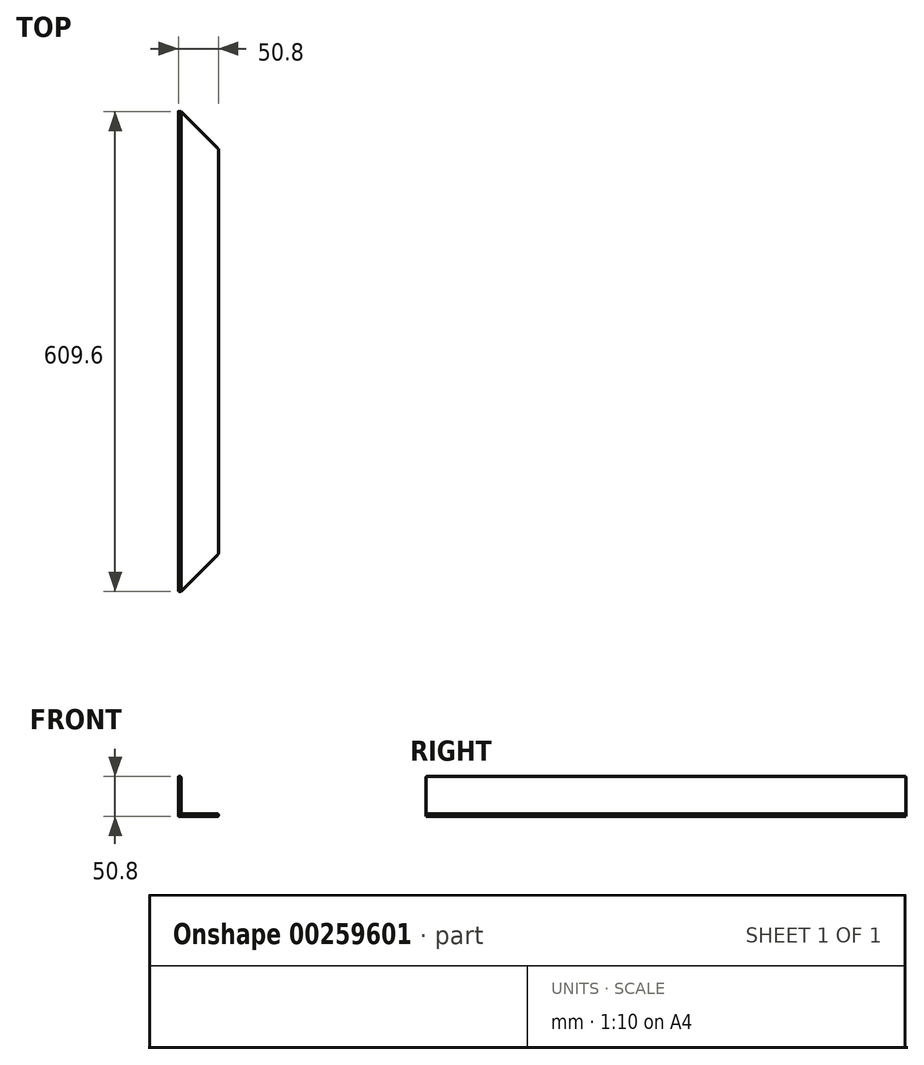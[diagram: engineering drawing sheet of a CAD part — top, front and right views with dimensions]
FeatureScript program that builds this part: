
annotation { "Feature Type Name" : "Feature", "Feature Type Description" : "" }
export const myFeature = defineFeature(function(context is Context, id is Id, definition is map)
    precondition{}
    {
        {
            var Q0;
            Q0=qCreatedBy(makeId("Front.planeOp"),FACE);
            var sketch = newSketch(context, id + "F0", { "sketchPlane" : qUnion([Q0])});
            skLineSegment(sketch, "E0", {"start": v(0, 0) * mm, "end": v(0, 50.8) * mm});
            skLineSegment(sketch, "E1", {"start": v(0, 50.8) * mm, "end": v(3.17, 50.8) * mm});
            skLineSegment(sketch, "E2", {"start": v(3.17, 50.8) * mm, "end": v(3.18, 3.17) * mm});
            skLineSegment(sketch, "E3", {"start": v(3.18, 3.17) * mm, "end": v(50.8, 3.18) * mm});
            skLineSegment(sketch, "E4", {"start": v(50.8, 3.18) * mm, "end": v(50.8, 0) * mm});
            skLineSegment(sketch, "E5", {"start": v(50.8, 0) * mm, "end": v(0, 0) * mm});
            skSolve(sketch);
        }
        {
            var Q0;
            Q0=makeQuery(id+"F0.imprint","IMPRINT",FACE,{"disambiguationData":[TD([[makeQuery(id+"F0.imprint","IMPRINT",EDGE,{"derivedFrom":sQuery(id+"F0.wireOp",EDGE,"E0")}),-1.0]])]});
            extrude(context, id + "F1", {"entities" : qUnion([Q0]), "depth" : 609.6 * mm});
        }
        {
            var Q0;
            Q0=makeQuery(id+"F1.opExtrude","SWEPT_FACE",FACE,{"disambiguationData":[OSD([sQuery(id+"F0.wireOp",EDGE,"E3")])]});
            var sketch = newSketch(context, id + "F2", { "sketchPlane" : qUnion([Q0])});
            skLineSegment(sketch, "E6", {"start": v(3.18, 0) * mm, "end": v(50.8, -47.63) * mm});
            skSolve(sketch);
        }
        {
            var Q0;
            Q0=makeQuery(id+"F1.opExtrude","SWEPT_FACE",FACE,{"disambiguationData":[OSD([sQuery(id+"F0.wireOp",EDGE,"E1")])]});
            fillet(context, id + "F3", {"entities" : qUnion([Q0]), "radius" : 1.27 * mm, "tangentPropagation" : true, "allowEdgeOverflow" : false});
        }
        {
            var Q0;
            {var subQ0=sQuery(id+"F2.wireOp",EDGE,"E6");Q0=makeQuery(id+"F2.imprint","IMPRINT",FACE,{"disambiguationData":[TD([[makeQuery(id+"F2.imprint","IMPRINT",EDGE,{"derivedFrom":subQ0}),1.0]])]});}
            extrude(context, id + "F4", {"entities" : qUnion([Q0]), "operationType" : NewBodyOperationType.REMOVE, "oppositeDirection" : true, "depth" : 3.8 * mm});
        }
        {
            var Q0;
            Q0=makeQuery(id+"F1.opExtrude","SWEPT_FACE",FACE,{"disambiguationData":[OSD([sQuery(id+"F0.wireOp",EDGE,"E3")])]});
            var sketch = newSketch(context, id + "F5", { "sketchPlane" : qUnion([Q0])});
            skLineSegment(sketch, "E7", {"start": v(3.17, -609.6) * mm, "end": v(50.8, -561.98) * mm});
            skSolve(sketch);
        }
        {
            var Q0;
            {var subQ0=sQuery(id+"F5.wireOp",EDGE,"E7");Q0=makeQuery(id+"F5.imprint","IMPRINT",FACE,{"disambiguationData":[TD([[makeQuery(id+"F5.imprint","IMPRINT",EDGE,{"derivedFrom":subQ0}),-1.0]])]});}
            extrude(context, id + "F6", {"entities" : qUnion([Q0]), "operationType" : NewBodyOperationType.REMOVE, "oppositeDirection" : true, "depth" : 3.8 * mm});
        }
        {
            var Q0;
            Q0=makeQuery(id+"F1.opExtrude","SWEPT_FACE",FACE,{"disambiguationData":[OSD([sQuery(id+"F0.wireOp",EDGE,"E4")])]});
            fillet(context, id + "F7", {"entities" : qUnion([Q0]), "radius" : 1.27 * mm, "tangentPropagation" : true, "allowEdgeOverflow" : false});
        }
        {
            var Q0;
            Q0=makeQuery(id+"F1.opExtrude","SWEPT_EDGE",EDGE,{"disambiguationData":[OSD([sQuery(id+"F0.wireOp",EDGE,"E0"),sQuery(id+"F0.wireOp",EDGE,"E5")])]});
            fillet(context, id + "F8", {"entities" : qUnion([Q0]), "radius" : 1.27 * mm, "tangentPropagation" : true, "allowEdgeOverflow" : false});
        }
    });
